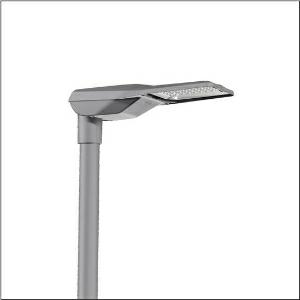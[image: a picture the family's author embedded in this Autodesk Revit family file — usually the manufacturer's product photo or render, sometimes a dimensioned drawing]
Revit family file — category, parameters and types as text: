
# Revit family: streetlight_sl_21_iq_mini___p1_0a_5xe2a31g08hb_5d57
name_source: partatom
category: Lighting Fixtures
units: mm (PartAtom-declared; Revit-internal decimal feet)

## family parameters
Cut with Voids When Loaded = No
Host = Face
Light Source = No
Part Type = Normal
Room Calculation Point = No
Round Connector Dimension = Use Diameter
Shared = No

## types (1)
- --- (1 x LED, 9450 lm, 70.9 W, 3000K)
    Apparent Load = 71 VA
    CIE Flux Codes = 21 50 90 100 100
    Color Rendering = 70
    Color Temperature = 3000K
    Default Elevation = 1800 mm
    Description = Streetlight SL 21 iQ mini, mast luminaire, primary light control with lens, of PMMA, primary optical cover: cover, of toughened safety glass, transparent, light distribution: P1.0a, light emission: direct distribution, primary light characteristic: asymmetric, installation type: post-top, side-entry, LED, High Power LED, rated luminous flux: 9.450lm, luminous efficacy: 133lm/W, light colour: 730, colour temperature: 3000K, control gear: iQ Street-Remote, control: Street-Remote, Auto-Match, Temp-Guard, Lumen-Switch, Night-Set, Smart-Wire, Light-Fading, Desk-Remote (wireless, voltage-free reading and setting of iQ features in the workshop via application-optimized NFC function/RFID function), optimised constant luminous flux control (CLO 2.0), pre-setting: linear dimming characteristic, mains connection: 220..240V, AC, 50/60Hz, start of lifetime: 71W, end of service life: 75W, reduction: 31W, luminaire housing, of diecast aluminium, powder-coated, Siteco® metallic grey (DB 702S), corrosivity category C5 mid according to DIN EN ISO 12944, please order mast flange separately, inclination adjustable: 0°, 5°, 10°, 15°, sealing non-destructively replaceable, multi-level sealing system, length: 628mm, width: 235mm, height: 110mm, mast flange for spigot size: 42mm (side-entry): 5XC10008XM4, 60/48mm (side-entry/post-top): 5XC10108XM2, 76/60mm (side-entry/post-top): 5XC10108XM1, mounting height: 4..8m, protection rating (complete): IP66, insulation class (complete): insulation class II (safety insulation), certification: CE, ENEC, ENEC+, VDE, impact resistance: IK10, permissible operating ambient temperature for outdoor applications: -40..+50°C, standard-compliant lighting for roads and squares, packaging unit: 1 piece

Light Distribution: P1.0a
    Height = 110 mm
    Lamp = 1 x LED
    Lamp Light Flux = 9450 lm
    Lamp Power = 70.9 W
    Lamp count = 1
    Length = 625 mm
    Luminous efficacy = 133 lm/W
    Manufacturer = Siteco
    ModVariant = No
    Model = 5XE2A31G08HB
    Number of Poles = 1
    OnlyDefault = Yes
    Power Factor = 1
    Product Name = Streetlight SL 21 iQ mini | P1.0a
    Product group = mast luminaire | pylon top
    ProductGroupID = 6100
    Protection Class = Protection class II
    Protection Degree = IP 66
    RLX_Detail_Level = 1
    RLX_Emergency_Light_Flux = 0 lm
    RLX_Emergency_Type = 0
    RLX_Emergency_Type_DB = No
    RlxData = <blob elided: 37521 chars, md5=3b06a839>
    Socket = socket
    Standby Power = 0 W
    System Light Flux = 9450 lm
    System Power = 71 W
    Type Comments = factory setting: luminous flux: 100 % | dim-lin: 254 | 711 mA
    Type Image = l_1003519.jpg
    URL = http://relux.com
    VarID = @adj_179135
    Voltage = 0 V
    Weight = 0.00 kg
    Width = 234 mm

## geometry (parser evidence)
native form markers: Blend x4, Sweep x10
no freeform markers — native parametric forms only
